# Revit family: Artek_Shelving_Kaari Wall Shelf_Kaari REB007
name_source: partatom
category: Furniture
revit_build: Autodesk Revit 2017 (Build: 20190508_0315(x64)
units: mm (PartAtom-declared; Revit-internal decimal feet)

## family parameters
Cut with Voids When Loaded = No
Host = Face
OmniClass Number = 23.40.20.27
OmniClass Title = Storage Shelving
Room Calculation Point = No
Shared = No

## types (3) — shared parameters
AssetType = Movable
BIMObjectName = Artek_Shelving_Kaari Wall Shelf round_Kaari REB007
Brand = Artek
Collection = Kaari Collection
ConvergoRefNr = 0190-2009-0040-FI
Designer = Ronan & Erwan Bouroullec
DurationUnit = Years
IfcExportAs = IfcFurnitureType
IfcExportType = SHELF
Manufacturer = Artek
ManufacturerName = Artek
ManufacturerURL = https://www.artek.fi
Material = Wood/Steel
NBSDescription = Shelf units
NBSReference = 45-35-80/310
Name = Kaari REB007
NominalDepth = 300 mm
NominalHeight = 350 mm
NominalWidth = 350 mm
Shape = Sculptured
Size = 350x300x350 mm
URL = https://www.artek.fi
Uniclass2 = Pr_40_30_78_77
Uniclass2015Description = Shelf units
Uniclass2015Reference = Pr_40_30_78_77
Version = 1
VersionDate = 11/3/2020
WarrantyDurationUnit = Years
zero-valued in all types: Default Elevation

## per-type parameters (varying)
| type | Category | Color | LegsMaterial | MainColor | ModelNumber | ShelfFrameMaterial | ShelfTopMaterial |
| Kaari Shelf REB007 - Blue | Shelves | Blue | Black oak | Blue | 28503215 | ABS Red | Linoleum blue |
| Kaari Shelf REB007 - Black | Shelving | Black | Natural oak, with protective varnish | Black | 28503212 | ABS | Linoleum black |
| Kaari Shelf REB007 - Red | Shelves | Red | Black oak | Red | 28503214 | ABS | Linoleum red |

note: column(s) folded — value = type name in every type: Model

## geometry (parser evidence)
native form markers: Sweep x6
no freeform markers — native parametric forms only
